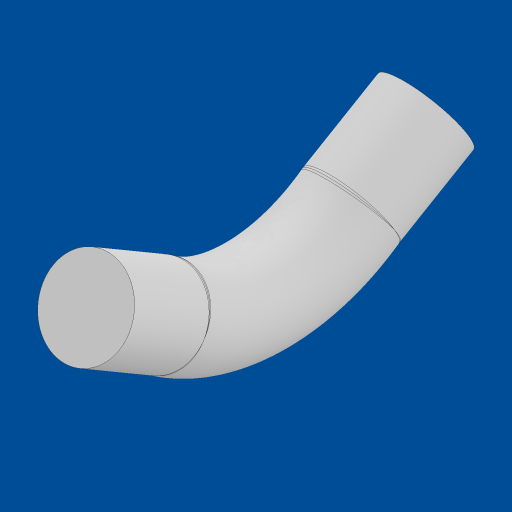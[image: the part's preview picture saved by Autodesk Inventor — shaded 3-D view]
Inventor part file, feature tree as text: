
AUTODESK INVENTOR PART (.ipt)
format: ipt  version: 2023 (Build 270158000, 158)  size: 156,672 bytes
history: native  units: mm
features: sketch x5, plane x2, extrude x2, sweep x1
ambient origin geometry x8: Origin, YZ Plane, XZ Plane, XY Plane, X Axis, Y Axis, Z Axis, Center Point
bodies: Solid1 (feature_tree)
feature tree (10):
  sketch  "Sketch1"  dims[d4=5.5mm d5=50.0mm d6=11.0mm]
  plane  "Work Plane2"
  sketch  "Sketch2"  dims[d7=11.0mm d8=0.0mm d9=11.0mm]
  extrude  "Extrusion1"  Depth=11.0mm
  plane  "Work Plane3"
  extrude  "Extrusion2"  Depth=11.0mm
  sweep  "Sweep1"
  sketch  "Sketch5"  dims[d17=5.5mm]
  sketch  "Sketch6"  dims[d18=5.5mm d19=11.0mm d20=11.0mm]
  sketch  "Sketch3"  dims[d10=11.0mm d11=0.0mm d12=0.0mm d13=0.0mm]
